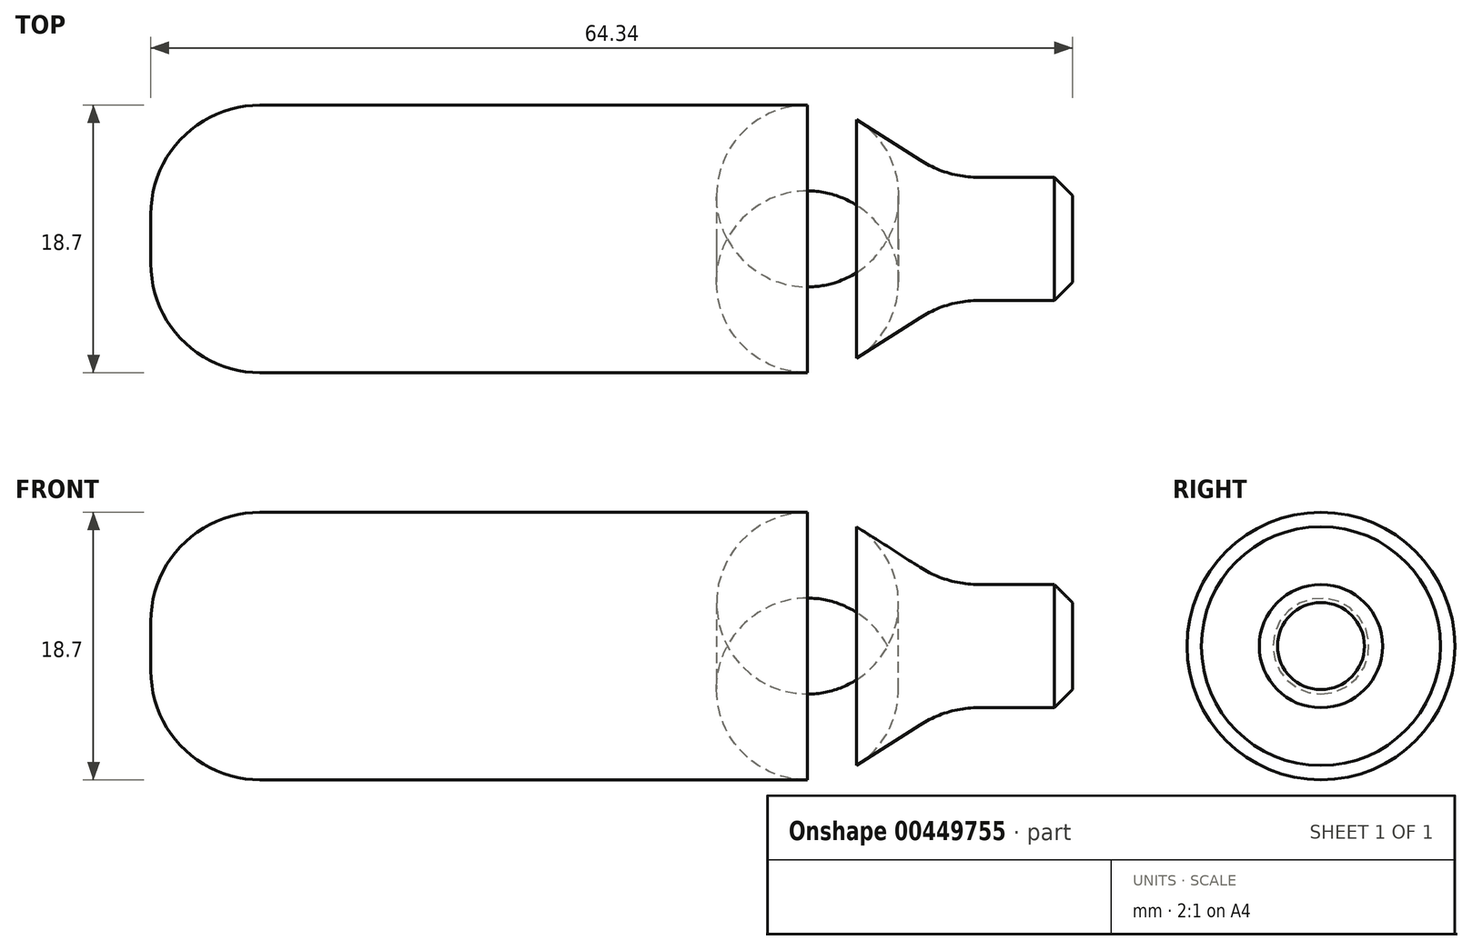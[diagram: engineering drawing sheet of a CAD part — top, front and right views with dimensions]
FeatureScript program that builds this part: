
annotation { "Feature Type Name" : "Feature", "Feature Type Description" : "" }
export const myFeature = defineFeature(function(context is Context, id is Id, definition is map)
    precondition{}
    {
        {
            var Q0;
            Q0=qCreatedBy(makeId("Front.planeOp"),FACE);
            var sketch = newSketch(context, id + "F0", { "sketchPlane" : qUnion([Q0])});
            skLineSegment(sketch, "E0", {"start": v(0, 0) * mm, "end": v(0, 4.3) * mm});
            skLineSegment(sketch, "E1", {"start": v(0, 4.3) * mm, "end": v(-6.53, 4.3) * mm});
            skLineSegment(sketch, "E2", {"start": v(-10.64, 5.5) * mm, "end": v(-15.07, 8.34) * mm});
            skLineSegment(sketch, "E3", {"start": v(-18.5, 9.35) * mm, "end": v(-56.72, 9.35) * mm});
            skLineSegment(sketch, "E4", {"start": v(-64.34, 1.73) * mm, "end": v(-64.34, 0) * mm});
            skLineSegment(sketch, "E5", {"start": v(-64.34, 0) * mm, "end": v(0, 0) * mm});
            skPoint(sketch, "E6.visualSharp", {"position": v(-64.34, 9.35) * mm});
            skArc(sketch, "E6.filletArc", {"start": v(-56.72, 9.35) * mm, "mid": v(-62.1, 7.12) * mm, "end": v(-64.34, 1.73) * mm});
            skPoint(sketch, "E7.visualSharp", {"position": v(-16.64, 9.35) * mm});
            skArc(sketch, "E7.filletArc", {"start": v(-15.07, 8.34) * mm, "mid": v(-16.71, 9.1) * mm, "end": v(-18.5, 9.35) * mm});
            skPoint(sketch, "E8.visualSharp", {"position": v(-8.76, 4.3) * mm});
            skArc(sketch, "E8.filletArc", {"start": v(-10.64, 5.5) * mm, "mid": v(-8.67, 4.61) * mm, "end": v(-6.53, 4.3) * mm});
            skSolve(sketch);
        }
        {
            var Q0;
            Q0 = qSketchRegion(id + "F0", true);
            var Q1;
            Q1=sQuery(id+"F0.wireOp",EDGE,"E5");
            revolve(context, id + "F1", {"entities" : qUnion([Q0]), "axis" : qUnion([Q1]), "revolveType" : RevolveType.FULL});
        }
        {
            var Q0;
            Q0=makeQuery(id+"F1.opRevolve","SWEPT_EDGE",EDGE,{"disambiguationData":[OSD([sQuery(id+"F0.wireOp",EDGE,"E0"),sQuery(id+"F0.wireOp",EDGE,"E1")])]});
            chamfer(context, id + "F2", {"entities" : qUnion([Q0]), "width" : 1.27 * mm, "tangentPropagation" : true});
        }
    });
